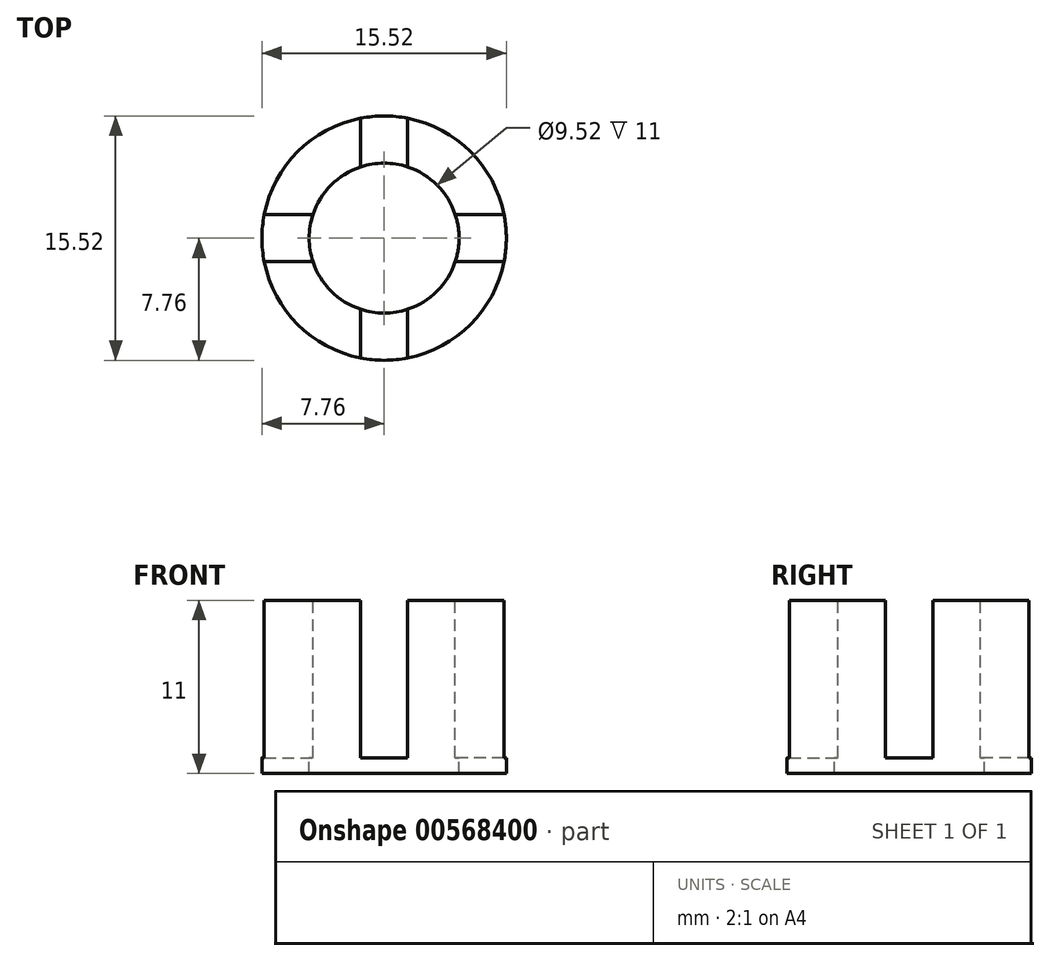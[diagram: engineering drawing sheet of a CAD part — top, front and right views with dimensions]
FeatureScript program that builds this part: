
annotation { "Feature Type Name" : "Feature", "Feature Type Description" : "" }
export const myFeature = defineFeature(function(context is Context, id is Id, definition is map)
    precondition{}
    {
        {
            var Q0;
            Q0=qCreatedBy(makeId("Front.planeOp"),FACE);
            var sketch = newSketch(context, id + "F0", { "sketchPlane" : qUnion([Q0])});
            skLineSegment(sketch, "E0", {"start": v(-7.76, 23) * mm, "end": v(-7.76, 34) * mm});
            skLineSegment(sketch, "E1", {"start": v(-7.76, 34) * mm, "end": v(-4.76, 34) * mm});
            skLineSegment(sketch, "E2", {"start": v(-7.76, 23) * mm, "end": v(-4.76, 23) * mm});
            skLineSegment(sketch, "E3", {"start": v(0, 37.35) * mm, "end": v(0, 21.35) * mm});
            skLineSegment(sketch, "E4", {"start": v(-4.76, 34) * mm, "end": v(-4.76, 23) * mm});
            skSolve(sketch);
        }
        {
            var Q0;
            Q0 = qSketchRegion(id + "F0", true);
            var Q1;
            Q1=sQuery(id+"F0.wireOp",EDGE,"E3");
            revolve(context, id + "F1", {"entities" : qUnion([Q0]), "axis" : qUnion([Q1]), "revolveType" : RevolveType.FULL});
        }
        {
            var Q0;
            Q0=makeQuery(id+"F1.opRevolve","SWEPT_FACE",FACE,{"disambiguationData":[OSD([sQuery(id+"F0.wireOp",EDGE,"E1")])]});
            var sketch = newSketch(context, id + "F2", { "sketchPlane" : qUnion([Q0])});
            skLineSegment(sketch, "E5.bottom", {"start": v(-1.5, 9.22) * mm, "end": v(1.5, 9.22) * mm});
            skLineSegment(sketch, "E5.top", {"start": v(-1.5, 3.96) * mm, "end": v(1.5, 3.96) * mm});
            skLineSegment(sketch, "E5.left", {"start": v(-1.5, 9.22) * mm, "end": v(-1.5, 3.96) * mm});
            skLineSegment(sketch, "E5.right", {"start": v(1.5, 9.22) * mm, "end": v(1.5, 3.96) * mm});
            skLineSegment(sketch, "E6.1.0", {"start": v(-9.22, -1.5) * mm, "end": v(-3.96, -1.5) * mm});
            skLineSegment(sketch, "E6.1.1", {"start": v(-9.22, -1.5) * mm, "end": v(-9.22, 1.5) * mm});
            skLineSegment(sketch, "E6.1.2", {"start": v(-9.22, 1.5) * mm, "end": v(-3.96, 1.5) * mm});
            skLineSegment(sketch, "E6.1.3", {"start": v(-3.96, -1.5) * mm, "end": v(-3.96, 1.5) * mm});
            skLineSegment(sketch, "E6.2.0", {"start": v(1.5, -9.22) * mm, "end": v(1.5, -3.96) * mm});
            skLineSegment(sketch, "E6.2.1", {"start": v(1.5, -9.22) * mm, "end": v(-1.5, -9.22) * mm});
            skLineSegment(sketch, "E6.2.2", {"start": v(-1.5, -9.22) * mm, "end": v(-1.5, -3.96) * mm});
            skLineSegment(sketch, "E6.2.3", {"start": v(1.5, -3.96) * mm, "end": v(-1.5, -3.96) * mm});
            skLineSegment(sketch, "E6.3.0", {"start": v(9.22, 1.5) * mm, "end": v(3.96, 1.5) * mm});
            skLineSegment(sketch, "E6.3.1", {"start": v(9.22, 1.5) * mm, "end": v(9.22, -1.5) * mm});
            skLineSegment(sketch, "E6.3.2", {"start": v(9.22, -1.5) * mm, "end": v(3.96, -1.5) * mm});
            skLineSegment(sketch, "E6.3.3", {"start": v(3.96, 1.5) * mm, "end": v(3.96, -1.5) * mm});
            skPoint(sketch, "E6.center", {"position": v(0, 0) * mm});
            skSolve(sketch);
        }
        {
            var Q0;
            Q0 = qSketchRegion(id + "F2", true);
            extrude(context, id + "F3", {"entities" : qUnion([Q0]), "operationType" : NewBodyOperationType.REMOVE, "oppositeDirection" : true, "depth" : 10 * mm, "offsetDistance" : 25 * mm});
        }
    });
